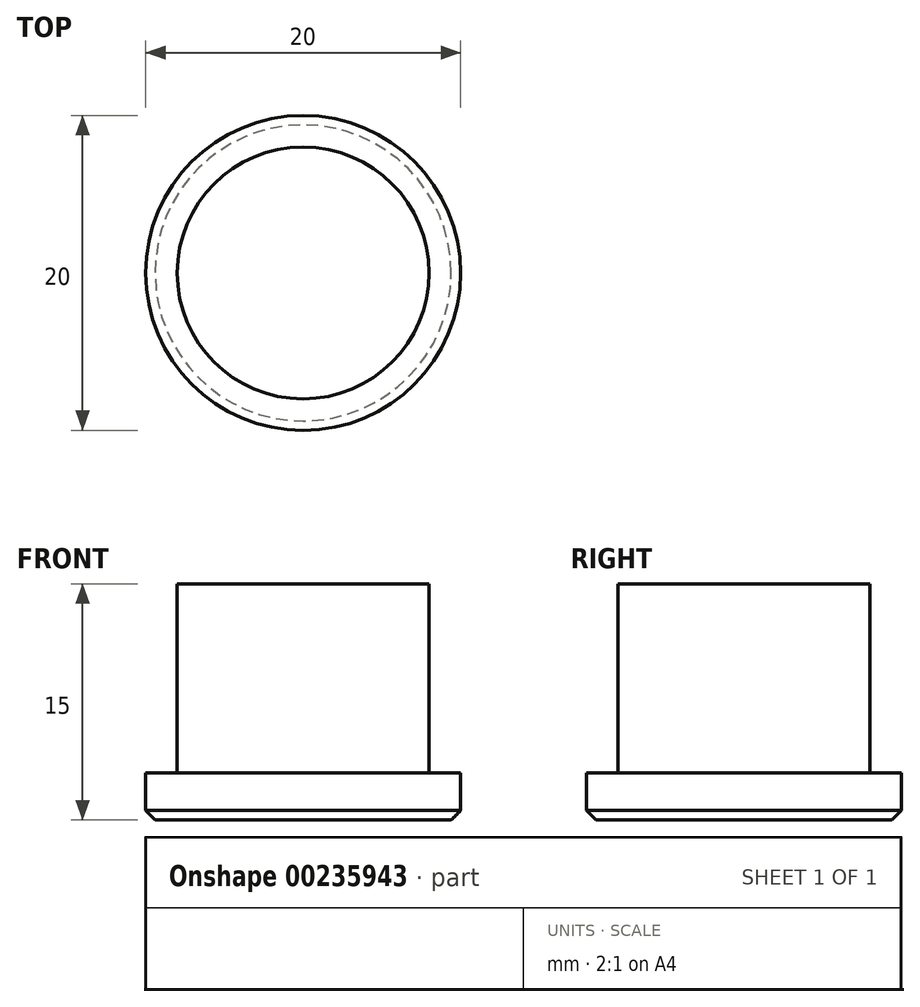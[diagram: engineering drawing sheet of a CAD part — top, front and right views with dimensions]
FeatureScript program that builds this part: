
annotation { "Feature Type Name" : "Feature", "Feature Type Description" : "" }
export const myFeature = defineFeature(function(context is Context, id is Id, definition is map)
    precondition{}
    {
        {
            var Q0;
            Q0=qCreatedBy(makeId("Front.planeOp"),FACE);
            var sketch = newSketch(context, id + "F0", { "sketchPlane" : qUnion([Q0])});
            skLineSegment(sketch, "E0", {"start": v(0, 0) * mm, "end": v(0, 15) * mm});
            skLineSegment(sketch, "E1", {"start": v(0, 15) * mm, "end": v(8, 15) * mm});
            skLineSegment(sketch, "E2", {"start": v(8, 15) * mm, "end": v(8, 3) * mm});
            skLineSegment(sketch, "E3", {"start": v(8, 3) * mm, "end": v(10, 3) * mm});
            skLineSegment(sketch, "E4", {"start": v(10, 3) * mm, "end": v(10, 0) * mm});
            skLineSegment(sketch, "E5", {"start": v(10, 0) * mm, "end": v(0, 0) * mm});
            skSolve(sketch);
        }
        {
            var Q0;
            Q0 = qSketchRegion(id + "F0", true);
            var Q1;
            Q1=sQuery(id+"F0.wireOp",EDGE,"E0");
            revolve(context, id + "F1", {"entities" : qUnion([Q0]), "axis" : qUnion([Q1]), "revolveType" : RevolveType.FULL});
        }
        {
            var Q0;
            Q0=makeQuery(id+"F1.opRevolve","SWEPT_EDGE",EDGE,{"disambiguationData":[OSD([sQuery(id+"F0.wireOp",EDGE,"E4"),sQuery(id+"F0.wireOp",EDGE,"E5")])]});
            chamfer(context, id + "F2", {"entities" : qUnion([Q0]), "chamferType" : ChamferType.OFFSET_ANGLE, "width" : .6 * mm, "oppositeDirection" : false, "angle" : 45 * degree, "tangentPropagation" : true});
        }
    });
